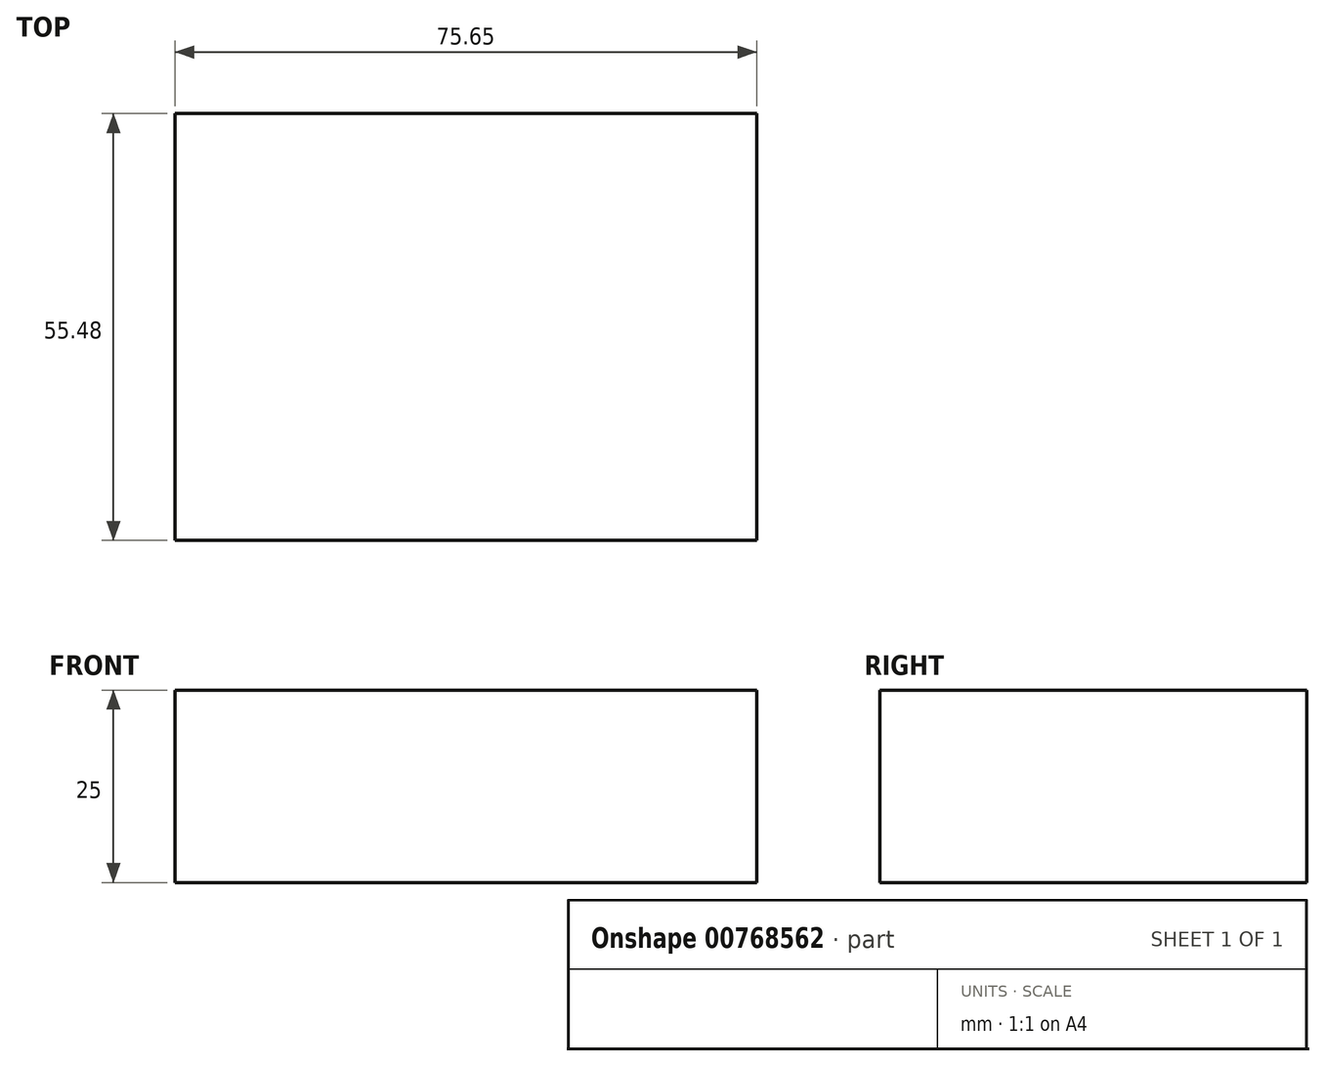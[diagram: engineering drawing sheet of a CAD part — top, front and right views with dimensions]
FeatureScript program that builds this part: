
annotation { "Feature Type Name" : "Feature", "Feature Type Description" : "" }
export const myFeature = defineFeature(function(context is Context, id is Id, definition is map)
    precondition{}
    {
        {
            var Q0;
            Q0=qCreatedBy(makeId("Top.planeOp"),FACE);
            var sketch = newSketch(context, id + "F0", { "sketchPlane" : qUnion([Q0])});
            skLineSegment(sketch, "E0.bottom", {"start": v(-19.1, 36.37) * mm, "end": v(56.54, 36.37) * mm});
            skLineSegment(sketch, "E0.top", {"start": v(-19.1, -19.1) * mm, "end": v(56.54, -19.1) * mm});
            skLineSegment(sketch, "E0.left", {"start": v(-19.1, 36.37) * mm, "end": v(-19.1, -19.1) * mm});
            skLineSegment(sketch, "E0.right", {"start": v(56.54, 36.37) * mm, "end": v(56.54, -19.1) * mm});
            skSolve(sketch);
        }
        {
            var Q0;
            Q0=makeQuery(id+"F0.imprint","IMPRINT",FACE,{"disambiguationData":[TD([[makeQuery(id+"F0.imprint","IMPRINT",EDGE,{"derivedFrom":sQuery(id+"F0.wireOp",EDGE,"E0.bottom")}),-1.0]])]});
            var Q1;
            Q1 = qSketchRegion(id + "FCVXkPTXXLT3AmY_1", true);
            extrude(context, id + "F1", {"entities" : qUnion([Q0, Q1]), "depth" : 25 * mm, "offsetDistance" : 25 * mm});
        }
    });
